# Revit family: Doors_Pruso_LK78X_Double-Sash_Inward-Opening
name_source: partatom
category: Doors
revit_build: Autodesk Revit 2018 (Build: 20170223_1515(x64)
units: mm (PartAtom-declared; Revit-internal decimal feet)

## family parameters
Always vertical = Yes
Cut with Voids When Loaded = No
Host = Wall
OmniClass Number = 23.30.10.00
OmniClass Title = Doors
Room Calculation Point = No
Shared = No

## types (1)
- Doors_Pruso_LK78X_Double-Sash_Inward-Opening
    Assembly Code = B20
    Edition number = 1
    Frame Material = Default
    Function = Interior
    Handle Material = Aluminium - Purso - Aluminium
    Height = 2200 mm
    Keynote = 08 11 00
    Leaf Material = Default
    Manufacturer = Purso
    Model = LK78X door, inward opening
    Product Guid = 462efe47-6342-498e-98f1-1a7b068f90dd
    Product data url = https://www.bimobject.com
    URL = https://purso.fi
    Wall Closure = By host
    Width = 2000 mm

## geometry (parser evidence)
native form markers: Sweep x8
no freeform markers — native parametric forms only
